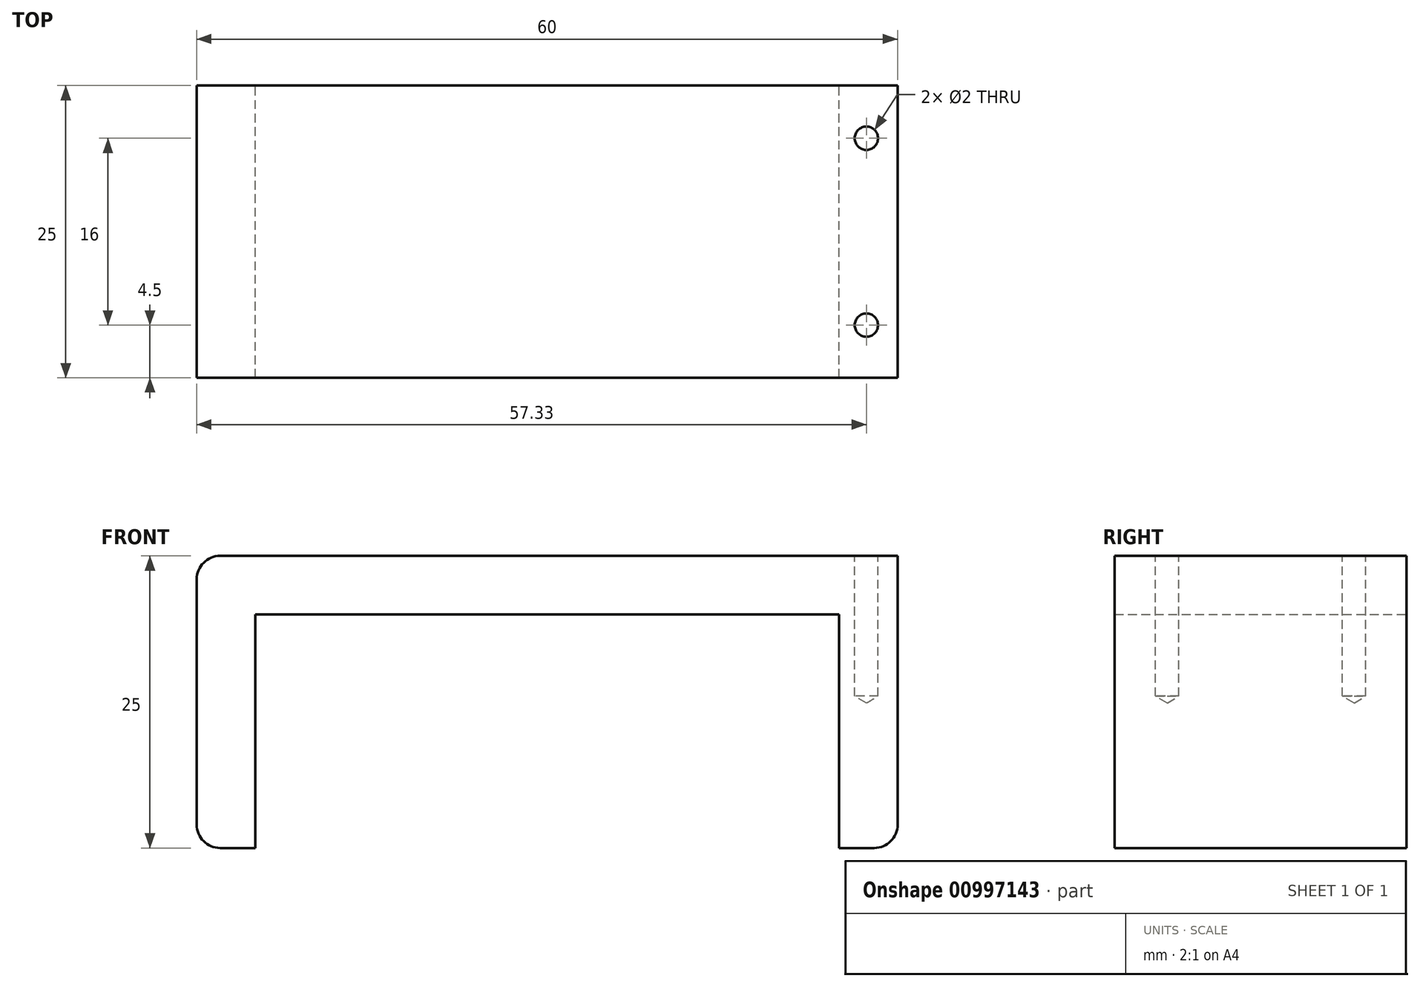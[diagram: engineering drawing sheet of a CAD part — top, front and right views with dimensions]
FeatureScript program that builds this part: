
annotation { "Feature Type Name" : "Feature", "Feature Type Description" : "" }
export const myFeature = defineFeature(function(context is Context, id is Id, definition is map)
    precondition{}
    {
        {
            var Q0;
            Q0=qCreatedBy(makeId("Front.planeOp"),FACE);
            var sketch = newSketch(context, id + "F0", { "sketchPlane" : qUnion([Q0])});
            skLineSegment(sketch, "E0.bottom", {"start": v(-29.83, 0) * mm, "end": v(30.17, 0) * mm});
            skLineSegment(sketch, "E0.top", {"start": v(-29.83, -25) * mm, "end": v(30.17, -25) * mm});
            skLineSegment(sketch, "E0.left", {"start": v(-29.83, 0) * mm, "end": v(-29.83, -25) * mm});
            skLineSegment(sketch, "E0.right", {"start": v(30.17, 0) * mm, "end": v(30.17, -25) * mm});
            skLineSegment(sketch, "E1.bottom", {"start": v(-24.83, -5) * mm, "end": v(25.17, -5) * mm});
            skLineSegment(sketch, "E1.top", {"start": v(-24.83, -25) * mm, "end": v(25.17, -25) * mm});
            skLineSegment(sketch, "E1.left", {"start": v(-24.83, -5) * mm, "end": v(-24.83, -25) * mm});
            skLineSegment(sketch, "E1.right", {"start": v(25.17, -5) * mm, "end": v(25.17, -25) * mm});
            skSolve(sketch);
        }
        {
            var Q0;
            Q0=makeQuery(id+"F0.imprint","IMPRINT",FACE,{"disambiguationData":[TD([[makeQuery(id+"F0.imprint","IMPRINT",EDGE,{"derivedFrom":sQuery(id+"F0.wireOp",EDGE,"5AY3xStQ-Lgd8-2JKP-TLlV-qz4FxI3wFyNV.top")}),1.0]])]});
            var Q1;
            Q1=makeQuery(id+"F0.imprint","IMPRINT",FACE,{"disambiguationData":[TD([[makeQuery(id+"F0.imprint","IMPRINT",EDGE,{"derivedFrom":sQuery(id+"F0.wireOp",EDGE,"E0.bottom")}),-1.0]])]});
            extrude(context, id + "F1", {"entities" : qUnion([Q0, Q1]), "endBound" : BoundingType.SYMMETRIC, "depth" : 25 * mm, "offsetDistance" : 25 * mm});
        }
        {
            var Q0;
            Q0=qCreatedBy(makeId("Top.planeOp"),FACE);
            var sketch = newSketch(context, id + "F2", { "sketchPlane" : qUnion([Q0])});
            skPoint(sketch, "E2", {"position": v(27.5, 8) * mm});
            skPoint(sketch, "E3", {"position": v(27.5, -8) * mm});
            skSolve(sketch);
        }
        {
            var Q0;
            Q0=makeQuery(id+"F1.opExtrude","SWEPT_EDGE",EDGE,{"disambiguationData":[OSD([sQuery(id+"F0.wireOp",EDGE,"E0.top"),sQuery(id+"F0.wireOp",EDGE,"E0.right")])]});
            var Q1;
            Q1=makeQuery(id+"F1.opExtrude","SWEPT_EDGE",EDGE,{"disambiguationData":[OSD([sQuery(id+"F0.wireOp",EDGE,"E0.top"),sQuery(id+"F0.wireOp",EDGE,"E0.left")])]});
            var Q2;
            Q2=makeQuery(id+"F1.opExtrude","SWEPT_EDGE",EDGE,{"disambiguationData":[OSD([sQuery(id+"F0.wireOp",EDGE,"E0.bottom"),sQuery(id+"F0.wireOp",EDGE,"E0.left")])]});
            fillet(context, id + "F3", {"entities" : qUnion([Q0, Q1, Q2]), "radius" : 2 * mm, "tangentPropagation" : true, "allowEdgeOverflow" : false});
        }
        {
            var Q0;
            Q0=sQuery(id+"F2.wireOp",VERTEX,"E2");
            var Q1;
            Q1=sQuery(id+"F2.wireOp",VERTEX,"E3");
            var Q2;
            Q2=makeQuery(id+"F1.opExtrude","SWEPT_BODY",BODY,{"disambiguationData":[OSD([sQuery(id+"F0.wireOp",EDGE,"E0.bottom"),sQuery(id+"F0.wireOp",EDGE,"E0.top"),sQuery(id+"F0.wireOp",EDGE,"E0.left"),sQuery(id+"F0.wireOp",EDGE,"E0.right"),sQuery(id+"F0.wireOp",EDGE,"E1.bottom"),sQuery(id+"F0.wireOp",EDGE,"E1.left"),sQuery(id+"F0.wireOp",EDGE,"E1.right")])]});
            hole(context, id + "F4", {"style" : HoleStyle.SIMPLE, "endStyle" : HoleEndStyle.BLIND, "holeDiameter" : 2 * mm, "majorDiameter" : 5 * mm, "holeDepth" : 12 * mm, "isTappedThrough" : true, "tappedDepth" : 12 * mm, "tapClearance" : 3, "locations" : qUnion([Q0, Q1]), "scope" : qUnion([Q2])});
        }
    });
